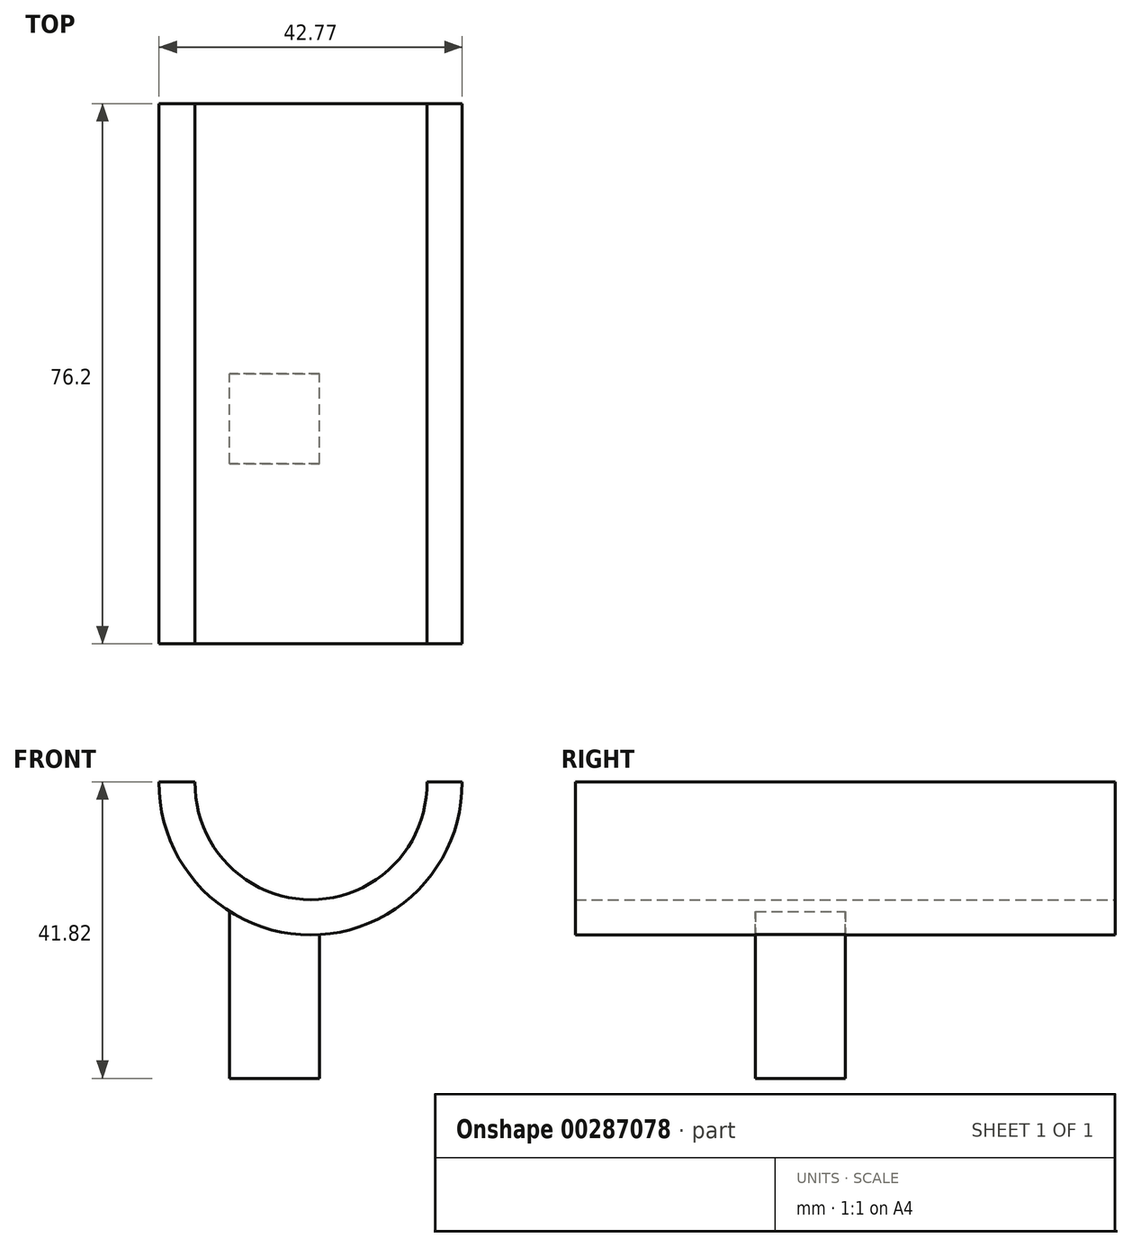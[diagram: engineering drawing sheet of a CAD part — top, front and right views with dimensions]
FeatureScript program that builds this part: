
annotation { "Feature Type Name" : "Feature", "Feature Type Description" : "" }
export const myFeature = defineFeature(function(context is Context, id is Id, definition is map)
    precondition{}
    {
        {
            var Q0;
            Q0=qCreatedBy(makeId("Front.planeOp"),FACE);
            var sketch = newSketch(context, id + "F0", { "sketchPlane" : qUnion([Q0])});
            skLineSegment(sketch, "E0", {"start": v(-60.72, 41.82) * mm, "end": v(-55.64, 41.82) * mm});
            skArc(sketch, "E1", {"start": v(-55.64, 41.82) * mm, "mid": v(-39.28, 25.2) * mm, "end": v(-22.91, 41.82) * mm});
            skLineSegment(sketch, "E2", {"start": v(-22.91, 41.82) * mm, "end": v(-17.95, 41.82) * mm});
            skArc(sketch, "E3", {"start": v(-60.72, 41.82) * mm, "mid": v(-39.34, 20.23) * mm, "end": v(-17.95, 41.82) * mm});
            skSolve(sketch);
        }
        {
            var Q0;
            Q0 = qSketchRegion(id + "F0", true);
            extrude(context, id + "F1", {"entities" : qUnion([Q0]), "depth" : 76.2 * mm});
        }
        {
            var Q0;
            Q0=qCreatedBy(makeId("Top.planeOp"),FACE);
            var sketch = newSketch(context, id + "F2", { "sketchPlane" : qUnion([Q0])});
            skLineSegment(sketch, "E4.bottom", {"start": v(-50.8, -38.1) * mm, "end": v(-38.1, -38.1) * mm});
            skLineSegment(sketch, "E4.top", {"start": v(-50.8, -50.8) * mm, "end": v(-38.1, -50.8) * mm});
            skLineSegment(sketch, "E4.left", {"start": v(-50.8, -38.1) * mm, "end": v(-50.8, -50.8) * mm});
            skLineSegment(sketch, "E4.right", {"start": v(-38.1, -38.1) * mm, "end": v(-38.1, -50.8) * mm});
            skSolve(sketch);
        }
        {
            var Q0;
            Q0 = qSketchRegion(id + "F2", true);
            extrude(context, id + "F3", {"entities" : qUnion([Q0]), "operationType" : NewBodyOperationType.ADD, "depth" : 23.62 * mm});
        }
    });
